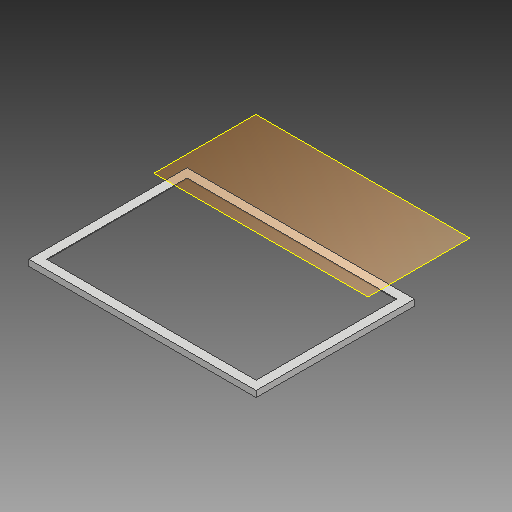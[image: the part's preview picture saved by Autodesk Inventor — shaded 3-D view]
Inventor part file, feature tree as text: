
AUTODESK INVENTOR PART (.ipt)
format: ipt  version: 2017 (Build 210142000, 142)  size: 119,296 bytes
history: native  units: mm
features: plane x4, other x3, sketch x2, extrude x2, reference x2, chamfer x1
ambient origin geometry x8: Origin, YZ Plane, XZ Plane, XY Plane, X Axis, Y Axis, Z Axis, Center Point
bodies: Body1 (feature_tree)
feature tree (14):
  plane  "Arbeitsebene1"
  sketch  "Skizze1"  dims[d0=0.1mm d1=0.1mm]
  plane  "Arbeitsebene2"
  plane  "Arbeitsebene3"
  plane  "Arbeitsebene4"
  extrude  "Extrusion2"  Depth=0.1mm
  extrude  "Extrusion3"  Depth=4.0mm
  chamfer  "Fase1"  Distance=4.0mm
  reference  "Referenz1"
  sketch  "Skizze2"  dims[d2=0.1mm d3=0.1mm d6=4.0mm d7=4.0mm d8=4.0mm d9=4.0mm d10=10.0mm d11=0.0mm d12=10.0mm d13=0.0mm d14=2.4mm d15=2.0mm d16=45.0deg]
  reference  "Referenz2"
  other  "<userpath>\Dropbox\Elektronik\aXe_Dashboard240XL\Gehäuse\DisplayDummyAuschnitt.iam"
  other  "DisplayDummyAuschnitt.iam"
  other  "DisplayDummy:1"
